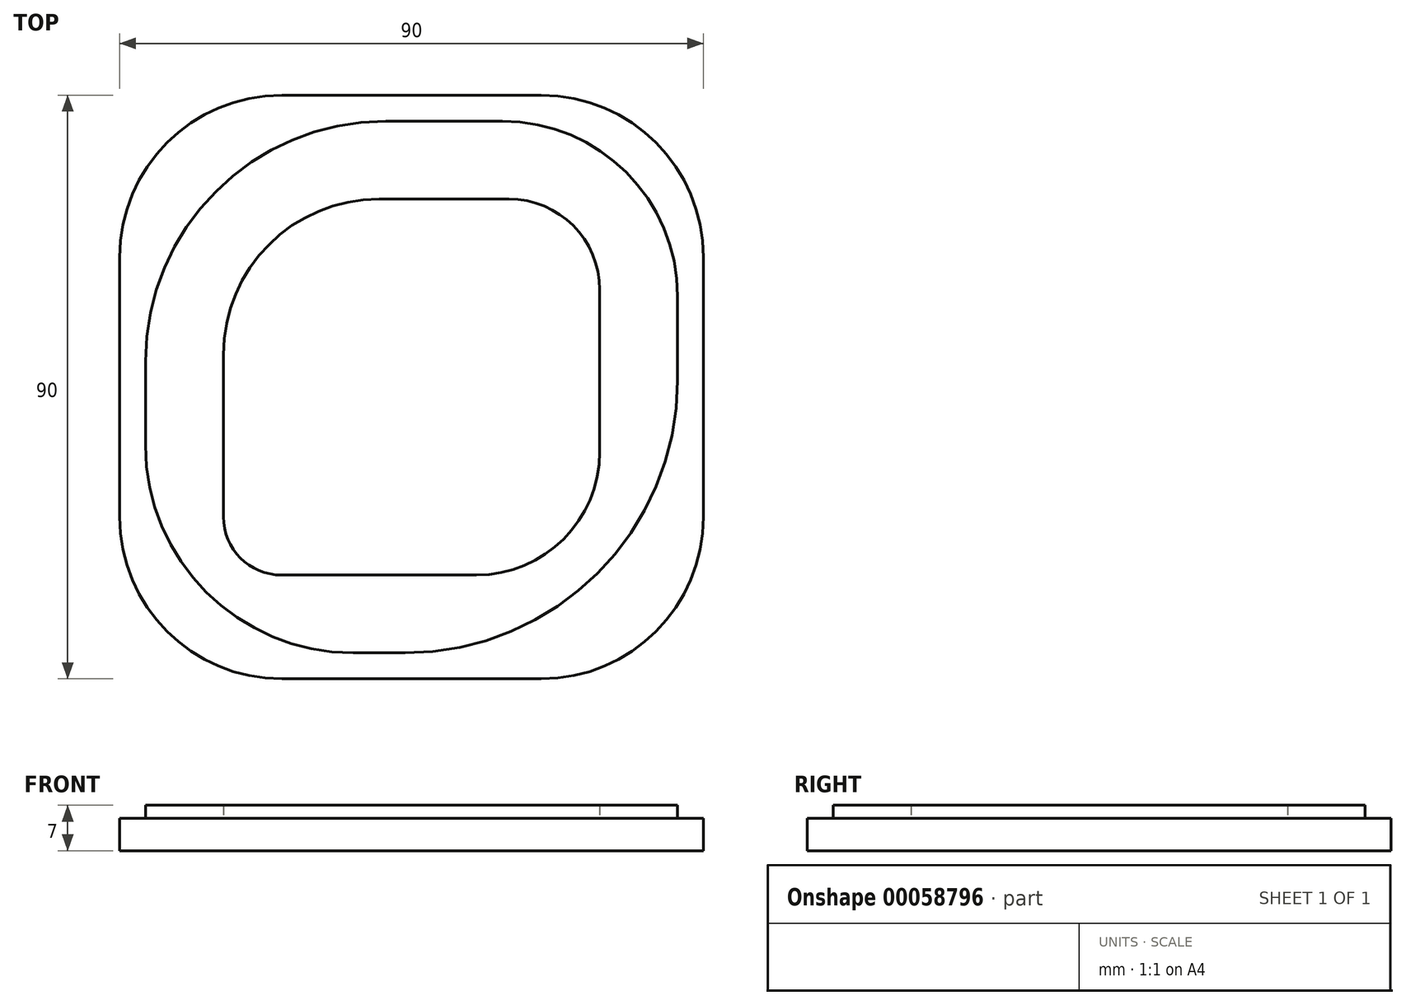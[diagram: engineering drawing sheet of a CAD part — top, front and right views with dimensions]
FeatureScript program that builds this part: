
annotation { "Feature Type Name" : "Feature", "Feature Type Description" : "" }
export const myFeature = defineFeature(function(context is Context, id is Id, definition is map)
    precondition{}
    {
        {
            var Q0;
            Q0=qCreatedBy(makeId("Top.planeOp"),FACE);
            var sketch = newSketch(context, id + "F0", { "sketchPlane" : qUnion([Q0])});
            skLineSegment(sketch, "E0.bottom", {"start": v(-45, 45) * mm, "end": v(45, 45) * mm});
            skLineSegment(sketch, "E0.top", {"start": v(-45, -45) * mm, "end": v(45, -45) * mm});
            skLineSegment(sketch, "E0.left", {"start": v(-45, 45) * mm, "end": v(-45, -45) * mm});
            skLineSegment(sketch, "E0.right", {"start": v(45, 45) * mm, "end": v(45, -45) * mm});
            skPoint(sketch, "E0.middle", {"position": v(0, 0) * mm});
            skSolve(sketch);
        }
        {
            var Q0;
            Q0 = qSketchRegion(id + "F0", true);
            extrude(context, id + "F1", {"entities" : qUnion([Q0]), "depth" : 5 * mm});
        }
        {
            var Q0;
            Q0=makeQuery(id+"F1.opExtrude","CAP_FACE",FACE,{"disambiguationData":[OSD([sQuery(id+"F0.wireOp",EDGE,"E0.bottom"),sQuery(id+"F0.wireOp",EDGE,"E0.top"),sQuery(id+"F0.wireOp",EDGE,"E0.left"),sQuery(id+"F0.wireOp",EDGE,"E0.right")])],"isStart":false});
            var sketch = newSketch(context, id + "F2", { "sketchPlane" : qUnion([Q0])});
            skLineSegment(sketch, "E1.bottom", {"start": v(-4, 41) * mm, "end": v(14, 41) * mm});
            skLineSegment(sketch, "E1.top", {"start": v(-9, -41) * mm, "end": v(-1, -41) * mm});
            skLineSegment(sketch, "E1.left", {"start": v(-41, 4) * mm, "end": v(-41, -9) * mm});
            skLineSegment(sketch, "E1.right", {"start": v(41, 14) * mm, "end": v(41, 1) * mm});
            skPoint(sketch, "E1.middle", {"position": v(0, 0) * mm});
            skPoint(sketch, "E2.visualSharp", {"position": v(-41, 41) * mm});
            skArc(sketch, "E2.filletArc", {"start": v(-4, 41) * mm, "mid": v(-30.16, 30.16) * mm, "end": v(-41, 4) * mm});
            skPoint(sketch, "E3.visualSharp", {"position": v(41, 41) * mm});
            skArc(sketch, "E3.filletArc", {"start": v(41, 14) * mm, "mid": v(33.1, 33.1) * mm, "end": v(14, 41) * mm});
            skPoint(sketch, "E4.visualSharp", {"position": v(-41, -41) * mm});
            skArc(sketch, "E4.filletArc", {"start": v(-41, -9) * mm, "mid": v(-31.63, -31.63) * mm, "end": v(-9, -41) * mm});
            skPoint(sketch, "E5.visualSharp", {"position": v(41, -41) * mm});
            skArc(sketch, "E5.filletArc", {"start": v(-1, -41) * mm, "mid": v(28.7, -28.7) * mm, "end": v(41, 1) * mm});
            skLineSegment(sketch, "E6.bottom", {"start": v(-5, 29) * mm, "end": v(15, 29) * mm});
            skLineSegment(sketch, "E6.top", {"start": v(-20, -29) * mm, "end": v(10, -29) * mm});
            skLineSegment(sketch, "E6.left", {"start": v(-29, 5) * mm, "end": v(-29, -20) * mm});
            skLineSegment(sketch, "E6.right", {"start": v(29, 15) * mm, "end": v(29, -10) * mm});
            skPoint(sketch, "E7.visualSharp", {"position": v(-29, 29) * mm});
            skArc(sketch, "E7.filletArc", {"start": v(-5, 29) * mm, "mid": v(-21.97, 21.97) * mm, "end": v(-29, 5) * mm});
            skPoint(sketch, "E8.visualSharp", {"position": v(29, -29) * mm});
            skArc(sketch, "E8.filletArc", {"start": v(10, -29) * mm, "mid": v(23.44, -23.44) * mm, "end": v(29, -10) * mm});
            skPoint(sketch, "E9.visualSharp", {"position": v(29, 29) * mm});
            skArc(sketch, "E9.filletArc", {"start": v(29, 15) * mm, "mid": v(24.9, 24.9) * mm, "end": v(15, 29) * mm});
            skPoint(sketch, "E10.visualSharp", {"position": v(-29, -29) * mm});
            skArc(sketch, "E10.filletArc", {"start": v(-29, -20) * mm, "mid": v(-26.36, -26.36) * mm, "end": v(-20, -29) * mm});
            skSolve(sketch);
        }
        {
            var Q0;
            Q0=makeQuery(id+"F2.imprint","IMPRINT",FACE,{"disambiguationData":[TD([[makeQuery(id+"F2.imprint","IMPRINT",EDGE,{"derivedFrom":sQuery(id+"F2.wireOp",EDGE,"E1.bottom")}),-1.0]])]});
            extrude(context, id + "F3", {"entities" : qUnion([Q0]), "operationType" : NewBodyOperationType.ADD, "depth" : 2 * mm});
        }
        {
            var Q0;
            Q0=makeQuery(id+"F1.opExtrude","SWEPT_EDGE",EDGE,{"disambiguationData":[OSD([sQuery(id+"F0.wireOp",EDGE,"E0.top"),sQuery(id+"F0.wireOp",EDGE,"E0.left")])]});
            var Q1;
            Q1=makeQuery(id+"F1.opExtrude","SWEPT_EDGE",EDGE,{"disambiguationData":[OSD([sQuery(id+"F0.wireOp",EDGE,"E0.top"),sQuery(id+"F0.wireOp",EDGE,"E0.right")])]});
            var Q2;
            Q2=makeQuery(id+"F1.opExtrude","SWEPT_EDGE",EDGE,{"disambiguationData":[OSD([sQuery(id+"F0.wireOp",EDGE,"E0.bottom"),sQuery(id+"F0.wireOp",EDGE,"E0.right")])]});
            var Q3;
            Q3=makeQuery(id+"F1.opExtrude","SWEPT_EDGE",EDGE,{"disambiguationData":[OSD([sQuery(id+"F0.wireOp",EDGE,"E0.bottom"),sQuery(id+"F0.wireOp",EDGE,"E0.left")])]});
            fillet(context, id + "F4", {"entities" : qUnion([Q0, Q1, Q2, Q3]), "radius" : 25 * mm, "tangentPropagation" : true, "allowEdgeOverflow" : false});
        }
    });
